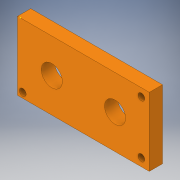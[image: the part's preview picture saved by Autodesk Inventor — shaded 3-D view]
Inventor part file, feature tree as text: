
AUTODESK INVENTOR PART (.ipt)
format: ipt  version: 2017 (Build 210142000, 142)  size: 176,640 bytes
history: native  units: in
note: dims shown in document units (in); Inventor stores cm internally (conversion verified against a paired STEP export)
features: sketch x12, extrude x11
ambient origin geometry x8: Origin, YZ Plane, XZ Plane, XY Plane, X Axis, Y Axis, Z Axis, Center Point
bodies: Solid1 (feature_tree)
feature tree (23):
  extrude  "Extrusion1"  Depth=1.3in
  sketch  "Sketch4"  dims[d2=0.25in d3=0.0in d14=0.2in d15=0.0in]
  extrude  "Extrusion4"  Depth=0.2in TaperAngle=0.0deg
  extrude  "Extrusion5"  Depth=0.65in
  extrude  "Extrusion6"  Depth=0.4in
  extrude  "Extrusion7"  Depth=0.3in TaperAngle=0.0deg
  extrude  "Extrusion9"  Depth=0.05in TaperAngle=0.0deg
  extrude  "Extrusion10"  Depth=0.13in
  extrude  "Extrusion11"  Depth=0.15in
  extrude  "Extrusion13"  Depth=0.15in
  extrude  "Extrusion14"  Depth=0.25in TaperAngle=0.0deg
  extrude  "Extrusion15"  Depth=0.1in
  sketch  "Sketch1"  dims[d0=2.3in d1=1.3in]
  sketch  "Sketch5"  dims[d16=0.4in d17=0.65in]
  sketch  "Sketch6"  dims[d18=0.6in d19=0.4in]
  sketch  "Sketch7"  dims[d20=1.05in d21=0.3in d22=0.0in]
  sketch  "Sketch8"  dims[d23=0.1in d24=0.0in d25=0.05in d26=0.0in]
  sketch  "Sketch10"  dims[d35=0.05in d36=0.0in d37=0.13in]
  sketch  "Sketch11"  dims[d38=0.13in d39=0.15in]
  sketch  "Sketch12"  dims[d40=0.15in d41=0.15in]
  sketch  "Sketch14"  dims[d42=0.15in d43=0.25in d44=0.0in]
  sketch  "Sketch15"  dims[d45=0.13in d46=0.1in]
  sketch  "Sketch16"  dims[d47=0.1in d48=0.25in d49=0.0in d55=0.65in d56=1.2in d57=0.4in d58=1.0in d59=0.0in d60=0.4in d61=1.0in d62=0.0in d63=2.0in d64=0.0in]
